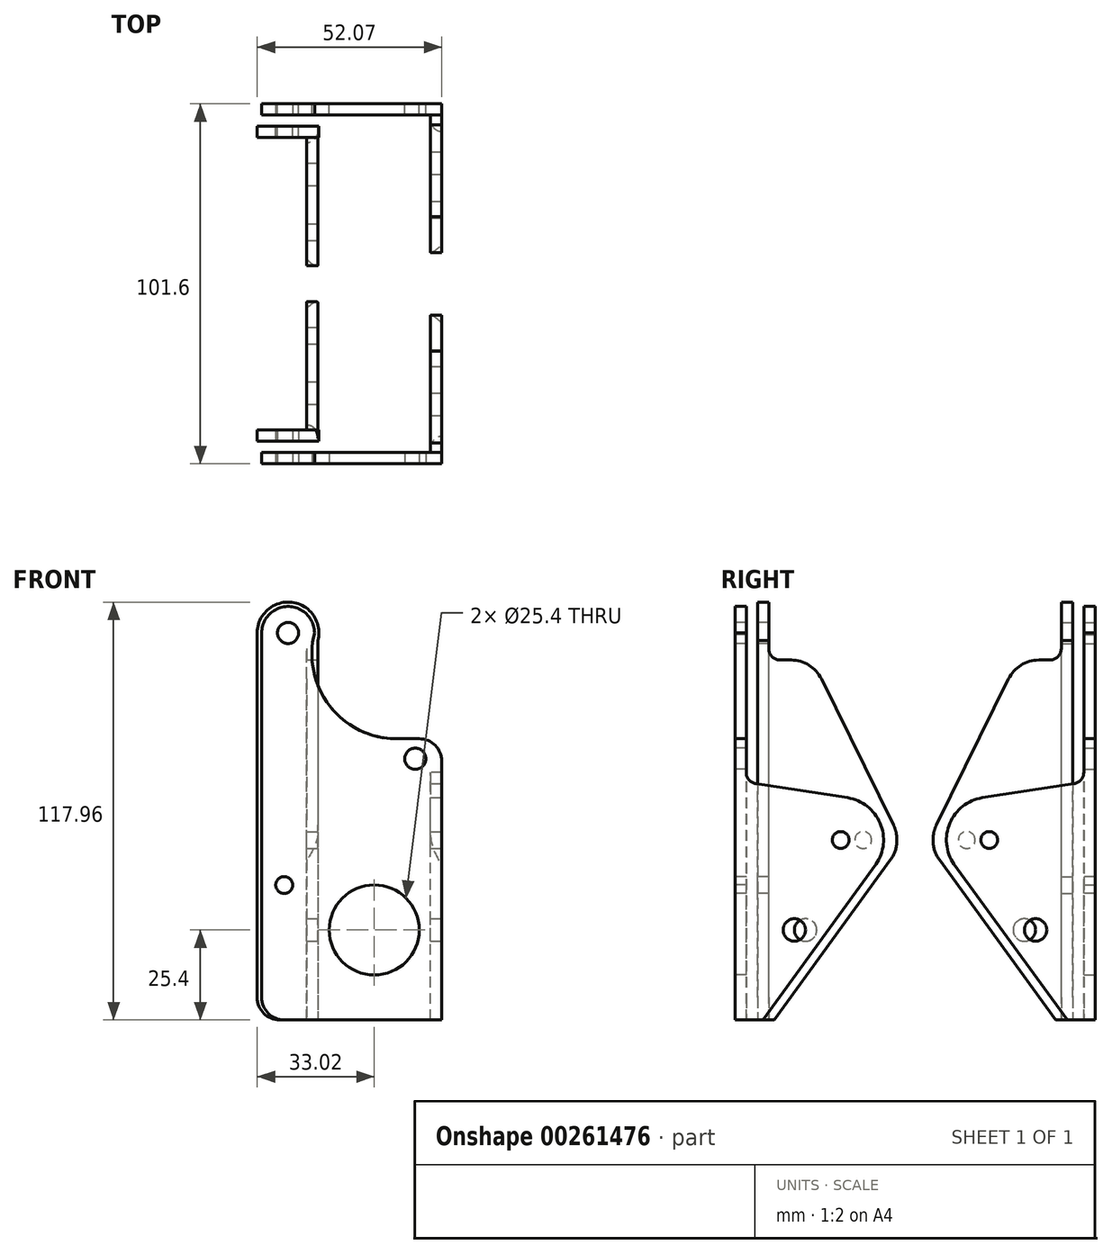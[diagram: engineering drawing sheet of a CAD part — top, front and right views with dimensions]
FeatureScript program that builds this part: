
annotation { "Feature Type Name" : "Feature", "Feature Type Description" : "" }
export const myFeature = defineFeature(function(context is Context, id is Id, definition is map)
    precondition{}
    {
        {
            var Q0;
            Q0=qCreatedBy(makeId("Front.planeOp"),FACE);
            var sketch = newSketch(context, id + "F18", { "sketchPlane" : qUnion([Q0])});
            skLineSegment(sketch, "E0", {"start": v(-19.05, 0) * mm, "end": v(0, 0) * mm});
            skLineSegment(sketch, "E1", {"start": v(0, 73.03) * mm, "end": v(0, 0) * mm});
            skPoint(sketch, "E2", {"position": v(-19.05, 25.4) * mm});
            skPoint(sketch, "E3.orphan", {"position": v(-50.8, 0) * mm});
            skCircle(sketch, "E4", {"center": v(-19.05, 25.4) * mm, "radius": 49.7 * mm, "construction": true});
            skCircle(sketch, "E5", {"center": v(-19.05, 25.4) * mm, "radius": 87.3 * mm, "construction": true});
            skLineSegment(sketch, "E6", {"start": v(-19.05, 25.4) * mm, "end": v(29.2, 226.66) * mm, "construction": true});
            skLineSegment(sketch, "E7", {"start": v(29.2, 226.66) * mm, "end": v(-19.05, 25.4) * mm, "construction": true});
            skLineSegment(sketch, "E8", {"start": v(-76.09, 222.15) * mm, "end": v(-19.05, 25.4) * mm, "construction": true});
            skPoint(sketch, "E9", {"position": v(-43.36, 109.25) * mm});
            skPoint(sketch, "E10", {"position": v(-7.46, 73.73) * mm});
            skLineSegment(sketch, "E11", {"start": v(-12.7, 79.38) * mm, "end": v(-6.35, 79.38) * mm});
            skArc(sketch, "E12", {"start": v(-12.7, 79.38) * mm, "mid": v(-31.61, 88.63) * mm, "end": v(-35.9, 109.25) * mm});
            skLineSegment(sketch, "E13", {"start": v(-50.8, 108.74) * mm, "end": v(-50.8, 6.35) * mm});
            skPoint(sketch, "E14.newPointA", {"position": v(0, 79.38) * mm});
            skArc(sketch, "E14.filletArc", {"start": v(0, 73.03) * mm, "mid": v(-1.86, 77.52) * mm, "end": v(-6.35, 79.38) * mm});
            skLineSegment(sketch, "E15", {"start": v(-6.35, 79.38) * mm, "end": v(0, 79.38) * mm});
            skLineSegment(sketch, "E16", {"start": v(0, 73.03) * mm, "end": v(0, 79.38) * mm});
            skArc(sketch, "E17", {"start": v(-36.44, 106.47) * mm, "mid": v(-43.14, 116.7) * mm, "end": v(-50.43, 106.87) * mm});
            skLineSegment(sketch, "E18", {"start": v(-44.45, 0) * mm, "end": v(0, 0) * mm});
            skArc(sketch, "E19", {"start": v(-50.8, 6.35) * mm, "mid": v(-48.94, 1.86) * mm, "end": v(-44.45, 0) * mm});
            skPoint(sketch, "E20", {"position": v(-44.45, 38.1) * mm});
            skSolve(sketch);
        }
        {
            var Q0;
            Q0=qCreatedBy(makeId("Right.planeOp"),FACE);
            var sketch = newSketch(context, id + "F19", { "sketchPlane" : qUnion([Q0])});
            skLineSegment(sketch, "E21", {"start": v(0, 0) * mm, "end": v(7.87, 0) * mm});
            skLineSegment(sketch, "E22", {"start": v(0, 79.38) * mm, "end": v(0, 0) * mm});
            skPoint(sketch, "E23", {"position": v(16.76, 25.4) * mm});
            skLineSegment(sketch, "E24", {"start": v(7.87, 0) * mm, "end": v(39.84, 44) * mm});
            skLineSegment(sketch, "E25", {"start": v(0, 0) * mm, "end": v(45.33, 0) * mm, "construction": true});
            skPoint(sketch, "E26", {"position": v(29.84, 50.8) * mm});
            skArc(sketch, "E27", {"start": v(39.84, 44) * mm, "mid": v(40.96, 55.56) * mm, "end": v(31.83, 62.73) * mm});
            skLineSegment(sketch, "E28", {"start": v(5.78, 66.73) * mm, "end": v(31.83, 62.73) * mm});
            skPoint(sketch, "E29", {"position": v(6.35, 69.85) * mm});
            skArc(sketch, "E30", {"start": v(3.18, 69.86) * mm, "mid": v(3.96, 67.76) * mm, "end": v(5.95, 66.7) * mm});
            skLineSegment(sketch, "E31", {"start": v(3.18, 69.86) * mm, "end": v(0, 69.86) * mm});
            skSolve(sketch);
        }
        {
            var Q0;
            Q0=makeQuery(id+"F18.imprint","IMPRINT",FACE,{"disambiguationData":[TD([[makeQuery(id+"F18.imprint","IMPRINT",EDGE,{"derivedFrom":sQuery(id+"F18.wireOp",EDGE,"E0")}),1.0]])]});
            var Q1;
            {var subQ5=sQuery(id+"F18.wireOp",EDGE,"E1");Q1=makeQuery(id+"F18.imprint","IMPRINT",FACE,{"disambiguationData":[TD([[makeQuery(id+"F18.imprint","IMPRINT",EDGE,{"derivedFrom":subQ5}),-1.0]])]});}
            extrude(context, id + "F0", {"entities" : qUnion([Q0, Q1]), "oppositeDirection" : true, "depth" : 3.17 * mm});
        }
        {
            var Q0;
            Q0=makeQuery(id+"F19.imprint","IMPRINT",FACE,{"disambiguationData":[TD([[makeQuery(id+"F19.imprint","IMPRINT",EDGE,{"derivedFrom":sQuery(id+"F19.wireOp",EDGE,"E21")}),1.0]])]});
            extrude(context, id + "F20", {"entities" : qUnion([Q0]), "operationType" : NewBodyOperationType.ADD, "oppositeDirection" : true, "depth" : 3.17 * mm});
        }
        {
            var Q0;
            Q0=sQuery(id+"F18.wireOp",VERTEX,"E2");
            var Q1;
            Q1=makeQuery(id+"F0.opExtrude","SWEPT_BODY",BODY,{"disambiguationData":[OSD([sQuery(id+"F18.wireOp",EDGE,"E0"),sQuery(id+"F18.wireOp",EDGE,"a3910ef7-181c-41b4-8af8-0729a50eed56"),sQuery(id+"F18.wireOp",EDGE,"8cec985d-35b8-4dd7-bd83-abb84eb66371"),sQuery(id+"F18.wireOp",EDGE,"E1")])]});
            hole(context, id + "F1", {"style" : HoleStyle.SIMPLE, "endStyle" : HoleEndStyle.THROUGH, "holeDiameter" : 25.4 * mm, "tappedDepth" : 12.7 * mm, "tapClearance" : 3, "locations" : qUnion([Q0]), "scope" : qUnion([Q1])});
        }
        {
            var Q0;
            Q0=sQuery(id+"F19.wireOp",VERTEX,"E23");
            var Q1;
            Q1=makeQuery(id+"F0.opExtrude","SWEPT_BODY",BODY,{"disambiguationData":[OSD([sQuery(id+"F18.wireOp",EDGE,"E0"),sQuery(id+"F18.wireOp",EDGE,"E1"),sQuery(id+"F18.wireOp",EDGE,"fa793434-73ff-4dec-b266-709bd48aa0cb"),sQuery(id+"F18.wireOp",EDGE,"E11"),sQuery(id+"F18.wireOp",EDGE,"299fa57f-807e-44ac-a0f5-9bb9c3f28c74"),sQuery(id+"F18.wireOp",EDGE,"E12"),sQuery(id+"F18.wireOp",EDGE,"E13"),sQuery(id+"F18.wireOp",EDGE,"E14.filletArc")])]});
            hole(context, id + "F21", {"style" : HoleStyle.SIMPLE, "endStyle" : HoleEndStyle.THROUGH, "holeDiameter" : 6.35 * mm, "tappedDepth" : 12.7 * mm, "tapClearance" : 3, "locations" : qUnion([Q0]), "scope" : qUnion([Q1])});
        }
        {
            var Q0;
            Q0=sQuery(id+"F19.wireOp",VERTEX,"E26");
            var Q1;
            Q1=makeQuery(id+"F0.opExtrude","SWEPT_BODY",BODY,{"disambiguationData":[OSD([sQuery(id+"F18.wireOp",EDGE,"E0"),sQuery(id+"F18.wireOp",EDGE,"E1"),sQuery(id+"F18.wireOp",EDGE,"fa793434-73ff-4dec-b266-709bd48aa0cb"),sQuery(id+"F18.wireOp",EDGE,"E11"),sQuery(id+"F18.wireOp",EDGE,"299fa57f-807e-44ac-a0f5-9bb9c3f28c74"),sQuery(id+"F18.wireOp",EDGE,"E12"),sQuery(id+"F18.wireOp",EDGE,"E13"),sQuery(id+"F18.wireOp",EDGE,"E14.filletArc")])]});
            hole(context, id + "F22", {"style" : HoleStyle.SIMPLE, "endStyle" : HoleEndStyle.THROUGH, "holeDiameter" : 4.76 * mm, "tappedDepth" : 12.7 * mm, "tapClearance" : 3, "locations" : qUnion([Q0]), "scope" : qUnion([Q1])});
        }
        {
            var Q0;
            Q0=sQuery(id+"F18.wireOp",VERTEX,"E9");
            var Q1;
            Q1=makeQuery(id+"F0.opExtrude","SWEPT_BODY",BODY,{"disambiguationData":[OSD([sQuery(id+"F18.wireOp",EDGE,"E0"),sQuery(id+"F18.wireOp",EDGE,"E1"),sQuery(id+"F18.wireOp",EDGE,"fa793434-73ff-4dec-b266-709bd48aa0cb"),sQuery(id+"F18.wireOp",EDGE,"E11"),sQuery(id+"F18.wireOp",EDGE,"299fa57f-807e-44ac-a0f5-9bb9c3f28c74"),sQuery(id+"F18.wireOp",EDGE,"E12"),sQuery(id+"F18.wireOp",EDGE,"E13"),sQuery(id+"F18.wireOp",EDGE,"E14.filletArc")])]});
            hole(context, id + "F2", {"style" : HoleStyle.SIMPLE, "endStyle" : HoleEndStyle.THROUGH, "holeDiameter" : 5.97 * mm, "tappedDepth" : 12.7 * mm, "tapClearance" : 3, "locations" : qUnion([Q0]), "scope" : qUnion([Q1])});
        }
        {
            var Q0;
            Q0=sQuery(id+"F18.wireOp",VERTEX,"E10");
            var Q1;
            Q1=makeQuery(id+"F0.opExtrude","SWEPT_BODY",BODY,{"disambiguationData":[OSD([sQuery(id+"F18.wireOp",EDGE,"E0"),sQuery(id+"F18.wireOp",EDGE,"E1"),sQuery(id+"F18.wireOp",EDGE,"fa793434-73ff-4dec-b266-709bd48aa0cb"),sQuery(id+"F18.wireOp",EDGE,"E11"),sQuery(id+"F18.wireOp",EDGE,"299fa57f-807e-44ac-a0f5-9bb9c3f28c74"),sQuery(id+"F18.wireOp",EDGE,"E12"),sQuery(id+"F18.wireOp",EDGE,"E13"),sQuery(id+"F18.wireOp",EDGE,"E14.filletArc")])]});
            hole(context, id + "F3", {"style" : HoleStyle.SIMPLE, "endStyle" : HoleEndStyle.THROUGH, "holeDiameter" : 5.97 * mm, "tappedDepth" : 12.7 * mm, "tapClearance" : 3, "locations" : qUnion([Q0]), "scope" : qUnion([Q1])});
        }
        {
            var Q0;
            Q0=makeQuery(id+"F18.imprint","IMPRINT",FACE,{"disambiguationData":[TD([[makeQuery(id+"F18.imprint","IMPRINT",EDGE,{"derivedFrom":sQuery(id+"F18.wireOp",EDGE,"E14.filletArc")}),-1.0]])]});
            extrude(context, id + "F4", {"entities" : qUnion([Q0]), "operationType" : NewBodyOperationType.REMOVE, "oppositeDirection" : true, "depth" : 25.4 * mm});
        }
        {
            var Q0;
            Q0=qCreatedBy(makeId("Front.planeOp"),FACE);
            cPlane(context, id + "F5", {"entities" : qUnion([Q0]), "cplaneType" : CPlaneType.OFFSET, "offset" : 50.8 * mm, "oppositeDirection" : true, "width" : 152.4 * mm, "height" : 152.4 * mm});
        }
        {
            var Q0;
            Q0=makeQuery(id+"F0.opExtrude","SWEPT_BODY",BODY,{"disambiguationData":[OSD([sQuery(id+"F18.wireOp",EDGE,"E0"),sQuery(id+"F18.wireOp",EDGE,"E1"),sQuery(id+"F18.wireOp",EDGE,"fa793434-73ff-4dec-b266-709bd48aa0cb"),sQuery(id+"F18.wireOp",EDGE,"E11"),sQuery(id+"F18.wireOp",EDGE,"299fa57f-807e-44ac-a0f5-9bb9c3f28c74"),sQuery(id+"F18.wireOp",EDGE,"E12"),sQuery(id+"F18.wireOp",EDGE,"E13"),sQuery(id+"F18.wireOp",EDGE,"E14.filletArc")])]});
            var Q1;
            Q1=qCreatedBy(id+"F5.planeOp",FACE);
            mirror(context, id + "F23", {"operationType" : NewBodyOperationType.ADD, "entities" : qUnion([Q0]), "mirrorPlane" : qUnion([Q1])});
        }
        {
            var Q0;
            Q0=qCreatedBy(makeId("Front.planeOp"),FACE);
            cPlane(context, id + "F6", {"entities" : qUnion([Q0]), "cplaneType" : CPlaneType.OFFSET, "offset" : 6.35 * mm, "oppositeDirection" : true, "width" : 152.4 * mm, "height" : 152.4 * mm});
        }
        {
            var Q0;
            Q0=qCreatedBy(id+"F6.planeOp",FACE);
            var sketch = newSketch(context, id + "F7", { "sketchPlane" : qUnion([Q0])});
            skLineSegment(sketch, "E32", {"start": v(-52.07, 119.54) * mm, "end": v(-52.07, 119.54) * mm});
            skLineSegment(sketch, "E33", {"start": v(-52.07, 6.35) * mm, "end": v(-52.07, 109.25) * mm});
            skLineSegment(sketch, "E34", {"start": v(-34.93, 107.06) * mm, "end": v(-34.93, 0) * mm});
            skLineSegment(sketch, "E35", {"start": v(-45.72, 0) * mm, "end": v(-34.93, 0) * mm});
            skPoint(sketch, "E36", {"position": v(-43.36, 109.25) * mm});
            skArc(sketch, "E37", {"start": v(-34.93, 107.06) * mm, "mid": v(-42.25, 117.89) * mm, "end": v(-52.07, 109.25) * mm});
            skArc(sketch, "E38", {"start": v(-52.07, 6.35) * mm, "mid": v(-50.21, 1.86) * mm, "end": v(-45.72, 0) * mm});
            skPoint(sketch, "E39.orphan", {"position": v(-52.07, 0) * mm});
            skSolve(sketch);
        }
        {
            var Q0;
            Q0=makeQuery(id+"F7.imprint","IMPRINT",FACE,{"disambiguationData":[TD([[makeQuery(id+"F7.imprint","IMPRINT",EDGE,{"derivedFrom":sQuery(id+"F7.wireOp",EDGE,"e57ed0a3-77e5-41d2-a626-6ee2ddd40895")}),1.0]])]});
            var Q1;
            Q1=makeQuery(id+"F7.imprint","IMPRINT",FACE,{"disambiguationData":[TD([[makeQuery(id+"F7.imprint","IMPRINT",EDGE,{"derivedFrom":sQuery(id+"F7.wireOp",EDGE,"E33")}),-1.0]])]});
            extrude(context, id + "F8", {"entities" : qUnion([Q0, Q1]), "oppositeDirection" : true, "depth" : 3.17 * mm});
        }
        {
            var Q0;
            Q0=sQuery(id+"F18.wireOp",VERTEX,"E9");
            var Q1;
            Q1=makeQuery(id+"F0.opExtrude","SWEPT_BODY",BODY,{"disambiguationData":[OSD([sQuery(id+"F18.wireOp",EDGE,"E1"),sQuery(id+"F18.wireOp",EDGE,"E11"),sQuery(id+"F18.wireOp",EDGE,"E12"),sQuery(id+"F18.wireOp",EDGE,"E13"),sQuery(id+"F18.wireOp",EDGE,"E14.filletArc"),sQuery(id+"F18.wireOp",EDGE,"E17"),sQuery(id+"F18.wireOp",EDGE,"E18")])]});
            var Q2;
            Q2=makeQuery(id+"F23.opPattern","COPY",BODY,{"derivedFrom":makeQuery(id+"F0.opExtrude","SWEPT_BODY",BODY,{"disambiguationData":[OSD([sQuery(id+"F18.wireOp",EDGE,"E1"),sQuery(id+"F18.wireOp",EDGE,"E11"),sQuery(id+"F18.wireOp",EDGE,"E12"),sQuery(id+"F18.wireOp",EDGE,"E13"),sQuery(id+"F18.wireOp",EDGE,"E14.filletArc"),sQuery(id+"F18.wireOp",EDGE,"E17"),sQuery(id+"F18.wireOp",EDGE,"E18")])]}),"instanceName":"1"});
            var Q3;
            Q3=makeQuery(id+"F8.opExtrude","SWEPT_BODY",BODY,{"disambiguationData":[OSD([sQuery(id+"F7.wireOp",EDGE,"E33"),sQuery(id+"F7.wireOp",EDGE,"E34"),sQuery(id+"F7.wireOp",EDGE,"E35"),sQuery(id+"F7.wireOp",EDGE,"E37")])]});
            hole(context, id + "F9", {"style" : HoleStyle.SIMPLE, "endStyle" : HoleEndStyle.THROUGH, "holeDiameter" : 5.97 * mm, "tappedDepth" : 12.7 * mm, "tapClearance" : 3, "locations" : qUnion([Q0]), "scope" : qUnion([Q1, Q2, Q3])});
        }
        {
            var Q0;
            Q0=qCreatedBy(makeId("Right.planeOp"),FACE);
            cPlane(context, id + "F10", {"entities" : qUnion([Q0]), "cplaneType" : CPlaneType.OFFSET, "offset" : 34.92 * mm, "oppositeDirection" : true, "width" : 152.4 * mm, "height" : 152.4 * mm});
        }
        {
            var Q0;
            Q0=qCreatedBy(id+"F10.planeOp",FACE);
            var sketch = newSketch(context, id + "F11", { "sketchPlane" : qUnion([Q0])});
            skLineSegment(sketch, "E40", {"start": v(11.06, 0) * mm, "end": v(11.06, 0) * mm});
            skLineSegment(sketch, "E41", {"start": v(15.88, 101.6) * mm, "end": v(12.7, 101.6) * mm});
            skLineSegment(sketch, "E42", {"start": v(6.35, 0) * mm, "end": v(6.35, 104.78) * mm});
            skLineSegment(sketch, "E43", {"start": v(43.9, 45.2) * mm, "end": v(11.06, 0) * mm});
            skPoint(sketch, "E44", {"position": v(19.94, 25.4) * mm});
            skPoint(sketch, "E45", {"position": v(36.2, 50.8) * mm});
            skArc(sketch, "E46", {"start": v(43.9, 45.2) * mm, "mid": v(45.69, 49.99) * mm, "end": v(44.74, 55) * mm});
            skArc(sketch, "E47", {"start": v(24.42, 96.28) * mm, "mid": v(20.9, 100.16) * mm, "end": v(15.88, 101.6) * mm});
            skLineSegment(sketch, "E48", {"start": v(24.42, 96.28) * mm, "end": v(44.74, 55) * mm});
            skArc(sketch, "E49", {"start": v(9.53, 104.77) * mm, "mid": v(10.45, 102.53) * mm, "end": v(12.7, 101.6) * mm});
            skLineSegment(sketch, "E50", {"start": v(6.39, 104.77) * mm, "end": v(6.35, 104.78) * mm});
            skLineSegment(sketch, "E51", {"start": v(9.53, 104.77) * mm, "end": v(6.39, 104.77) * mm});
            skLineSegment(sketch, "E52", {"start": v(6.35, 0) * mm, "end": v(11.06, 0) * mm});
            skSolve(sketch);
        }
        {
            var Q0;
            Q0=makeQuery(id+"F11.imprint","IMPRINT",FACE,{"disambiguationData":[TD([[makeQuery(id+"F11.imprint","IMPRINT",EDGE,{"derivedFrom":sQuery(id+"F11.wireOp",EDGE,"c2269cfa-445b-4eb1-8d0d-4ed57f7267c9")}),1.0]])]});
            var Q1;
            Q1=makeQuery(id+"F11.imprint","IMPRINT",FACE,{"disambiguationData":[TD([[makeQuery(id+"F11.imprint","IMPRINT",EDGE,{"derivedFrom":sQuery(id+"F11.wireOp",EDGE,"E41")}),1.0]])]});
            extrude(context, id + "F12", {"entities" : qUnion([Q0, Q1]), "operationType" : NewBodyOperationType.ADD, "oppositeDirection" : true, "depth" : 3.17 * mm});
        }
        {
            var Q0;
            Q0=sQuery(id+"F11.wireOp",VERTEX,"E46.center");
            var Q1;
            Q1=makeQuery(id+"F8.opExtrude","SWEPT_BODY",BODY,{"disambiguationData":[OSD([sQuery(id+"F7.wireOp",EDGE,"E33"),sQuery(id+"F7.wireOp",EDGE,"E34"),sQuery(id+"F7.wireOp",EDGE,"E35"),sQuery(id+"F7.wireOp",EDGE,"E37")])]});
            hole(context, id + "F13", {"style" : HoleStyle.SIMPLE, "endStyle" : HoleEndStyle.BLIND, "holeDiameter" : 4.78 * mm, "holeDepth" : 12.7 * mm, "tappedDepth" : 12.7 * mm, "tapClearance" : 3, "locations" : qUnion([Q0]), "scope" : qUnion([Q1])});
        }
        {
            var Q0;
            Q0=sQuery(id+"F11.wireOp",VERTEX,"E44");
            var Q1;
            Q1=makeQuery(id+"F8.opExtrude","SWEPT_BODY",BODY,{"disambiguationData":[OSD([sQuery(id+"F7.wireOp",EDGE,"E33"),sQuery(id+"F7.wireOp",EDGE,"E34"),sQuery(id+"F7.wireOp",EDGE,"E35"),sQuery(id+"F7.wireOp",EDGE,"E37")])]});
            hole(context, id + "F14", {"style" : HoleStyle.SIMPLE, "endStyle" : HoleEndStyle.BLIND, "holeDiameter" : 6.35 * mm, "holeDepth" : 12.7 * mm, "tappedDepth" : 12.7 * mm, "tapClearance" : 3, "locations" : qUnion([Q0]), "scope" : qUnion([Q1])});
        }
        {
            var Q0;
            Q0=sQuery(id+"F18.wireOp",VERTEX,"E20");
            var Q1;
            Q1=makeQuery(id+"F0.opExtrude","SWEPT_BODY",BODY,{"disambiguationData":[OSD([sQuery(id+"F18.wireOp",EDGE,"E1"),sQuery(id+"F18.wireOp",EDGE,"E11"),sQuery(id+"F18.wireOp",EDGE,"E12"),sQuery(id+"F18.wireOp",EDGE,"E13"),sQuery(id+"F18.wireOp",EDGE,"E14.filletArc"),sQuery(id+"F18.wireOp",EDGE,"E17"),sQuery(id+"F18.wireOp",EDGE,"E18"),sQuery(id+"F18.wireOp",EDGE,"E19")])]});
            var Q2;
            Q2=makeQuery(id+"F23.opPattern","COPY",BODY,{"derivedFrom":makeQuery(id+"F0.opExtrude","SWEPT_BODY",BODY,{"disambiguationData":[OSD([sQuery(id+"F18.wireOp",EDGE,"E1"),sQuery(id+"F18.wireOp",EDGE,"E11"),sQuery(id+"F18.wireOp",EDGE,"E12"),sQuery(id+"F18.wireOp",EDGE,"E13"),sQuery(id+"F18.wireOp",EDGE,"E14.filletArc"),sQuery(id+"F18.wireOp",EDGE,"E17"),sQuery(id+"F18.wireOp",EDGE,"E18"),sQuery(id+"F18.wireOp",EDGE,"E19")])]}),"instanceName":"1"});
            var Q3;
            Q3=makeQuery(id+"F8.opExtrude","SWEPT_BODY",BODY,{"disambiguationData":[OSD([sQuery(id+"F7.wireOp",EDGE,"E33"),sQuery(id+"F7.wireOp",EDGE,"E34"),sQuery(id+"F7.wireOp",EDGE,"E35"),sQuery(id+"F7.wireOp",EDGE,"E37"),sQuery(id+"F7.wireOp",EDGE,"E38")])]});
            hole(context, id + "F15", {"style" : HoleStyle.SIMPLE, "endStyle" : HoleEndStyle.THROUGH, "holeDiameter" : 4.78 * mm, "tappedDepth" : 12.7 * mm, "tapClearance" : 3, "locations" : qUnion([Q0]), "scope" : qUnion([Q1, Q2, Q3])});
        }
        {
            var Q0;
            Q0=makeQuery(id+"F8.opExtrude","SWEPT_BODY",BODY,{"disambiguationData":[OSD([sQuery(id+"F7.wireOp",EDGE,"E33"),sQuery(id+"F7.wireOp",EDGE,"E34"),sQuery(id+"F7.wireOp",EDGE,"E35"),sQuery(id+"F7.wireOp",EDGE,"E37"),sQuery(id+"F7.wireOp",EDGE,"E38")])]});
            var Q1;
            Q1=qCreatedBy(id+"F5.planeOp",FACE);
            mirror(context, id + "F16", {"entities" : qUnion([Q0]), "mirrorPlane" : qUnion([Q1])});
        }
        {
            var Q0;
            Q0=makeQuery(id+"F12.opExtrude","CAP_EDGE",EDGE,{"disambiguationData":[OSD([sQuery(id+"F11.wireOp",EDGE,"E43")])],"isStart":true});
            var Q1;
            Q1=makeQuery(id+"F16.opPattern","COPY",EDGE,{"derivedFrom":makeQuery(id+"F12.opExtrude","CAP_EDGE",EDGE,{"disambiguationData":[OSD([sQuery(id+"F11.wireOp",EDGE,"E43")])],"isStart":true}),"instanceName":"1"});
            var Q2;
            Q2=makeQuery(id+"F20.opExtrude","CAP_EDGE",EDGE,{"disambiguationData":[OSD([sQuery(id+"F19.wireOp",EDGE,"E24")])],"isStart":false});
            var Q3;
            Q3=makeQuery(id+"F23.opPattern","COPY",EDGE,{"derivedFrom":makeQuery(id+"F20.opExtrude","CAP_EDGE",EDGE,{"disambiguationData":[OSD([sQuery(id+"F19.wireOp",EDGE,"E24")])],"isStart":false}),"instanceName":"1"});
            fillet(context, id + "F17", {"entities" : qUnion([Q0, Q1, Q2, Q3]), "radius" : 3.17 * mm, "allowEdgeOverflow" : false});
        }
    });
